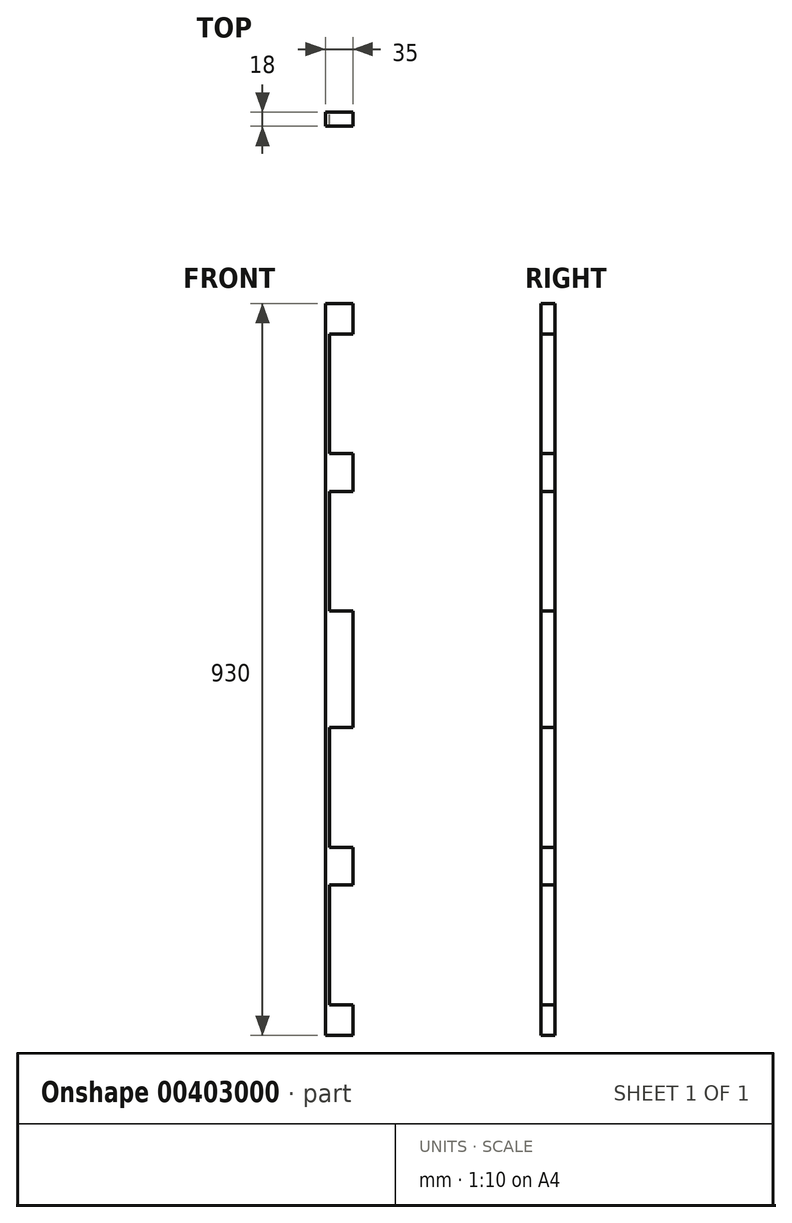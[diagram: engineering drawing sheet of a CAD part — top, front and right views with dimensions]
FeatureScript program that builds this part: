
annotation { "Feature Type Name" : "Feature", "Feature Type Description" : "" }
export const myFeature = defineFeature(function(context is Context, id is Id, definition is map)
    precondition{}
    {
        {
            var Q0;
            Q0=qCreatedBy(makeId("Front.planeOp"),FACE);
            var sketch = newSketch(context, id + "F0", { "sketchPlane" : qUnion([Q0])});
            skLineSegment(sketch, "E0.bottom", {"start": v(0, 0) * mm, "end": v(35, 0) * mm});
            skLineSegment(sketch, "E0.top", {"start": v(0, 930) * mm, "end": v(35, 930) * mm});
            skLineSegment(sketch, "E0.left", {"start": v(0, 0) * mm, "end": v(0, 930) * mm});
            skLineSegment(sketch, "E0.right", {"start": v(35, 0) * mm, "end": v(35, 39) * mm});
            skLineSegment(sketch, "E1.bottom", {"start": v(5, 891) * mm, "end": v(35, 891) * mm});
            skLineSegment(sketch, "E1.top", {"start": v(5, 739) * mm, "end": v(35, 739) * mm});
            skLineSegment(sketch, "E1.right", {"start": v(5, 891) * mm, "end": v(5, 739) * mm});
            skLineSegment(sketch, "E2.bottom", {"start": v(5, 391) * mm, "end": v(35, 391) * mm});
            skLineSegment(sketch, "E2.top", {"start": v(5, 239) * mm, "end": v(35, 239) * mm});
            skLineSegment(sketch, "E2.right", {"start": v(5, 391) * mm, "end": v(5, 239) * mm});
            skLineSegment(sketch, "E3.trimOffspring", {"start": v(35, 891) * mm, "end": v(35, 930) * mm});
            skLineSegment(sketch, "E4.trimOffspring", {"start": v(35, 391) * mm, "end": v(35, 539) * mm});
            skLineSegment(sketch, "E5.bottom", {"start": v(35, 691) * mm, "end": v(5, 691) * mm});
            skLineSegment(sketch, "E5.top", {"start": v(35, 539) * mm, "end": v(5, 539) * mm});
            skLineSegment(sketch, "E5.right", {"start": v(5, 691) * mm, "end": v(5, 539) * mm});
            skLineSegment(sketch, "E6.bottom", {"start": v(35, 191) * mm, "end": v(5, 191) * mm});
            skLineSegment(sketch, "E6.top", {"start": v(35, 39) * mm, "end": v(5, 39) * mm});
            skLineSegment(sketch, "E6.right", {"start": v(5, 191) * mm, "end": v(5, 39) * mm});
            skLineSegment(sketch, "E7.trimOffspring", {"start": v(35, 691) * mm, "end": v(35, 739) * mm});
            skLineSegment(sketch, "E8.trimOffspring", {"start": v(35, 191) * mm, "end": v(35, 239) * mm});
            skSolve(sketch);
        }
        {
            var Q0;
            Q0=makeQuery(id+"F0.imprint","IMPRINT",FACE,{"disambiguationData":[TD([[makeQuery(id+"F0.imprint","IMPRINT",EDGE,{"derivedFrom":sQuery(id+"F0.wireOp",EDGE,"E0.bottom")}),1.0]])]});
            extrude(context, id + "F1", {"entities" : qUnion([Q0]), "depth" : 18 * mm});
        }
    });
